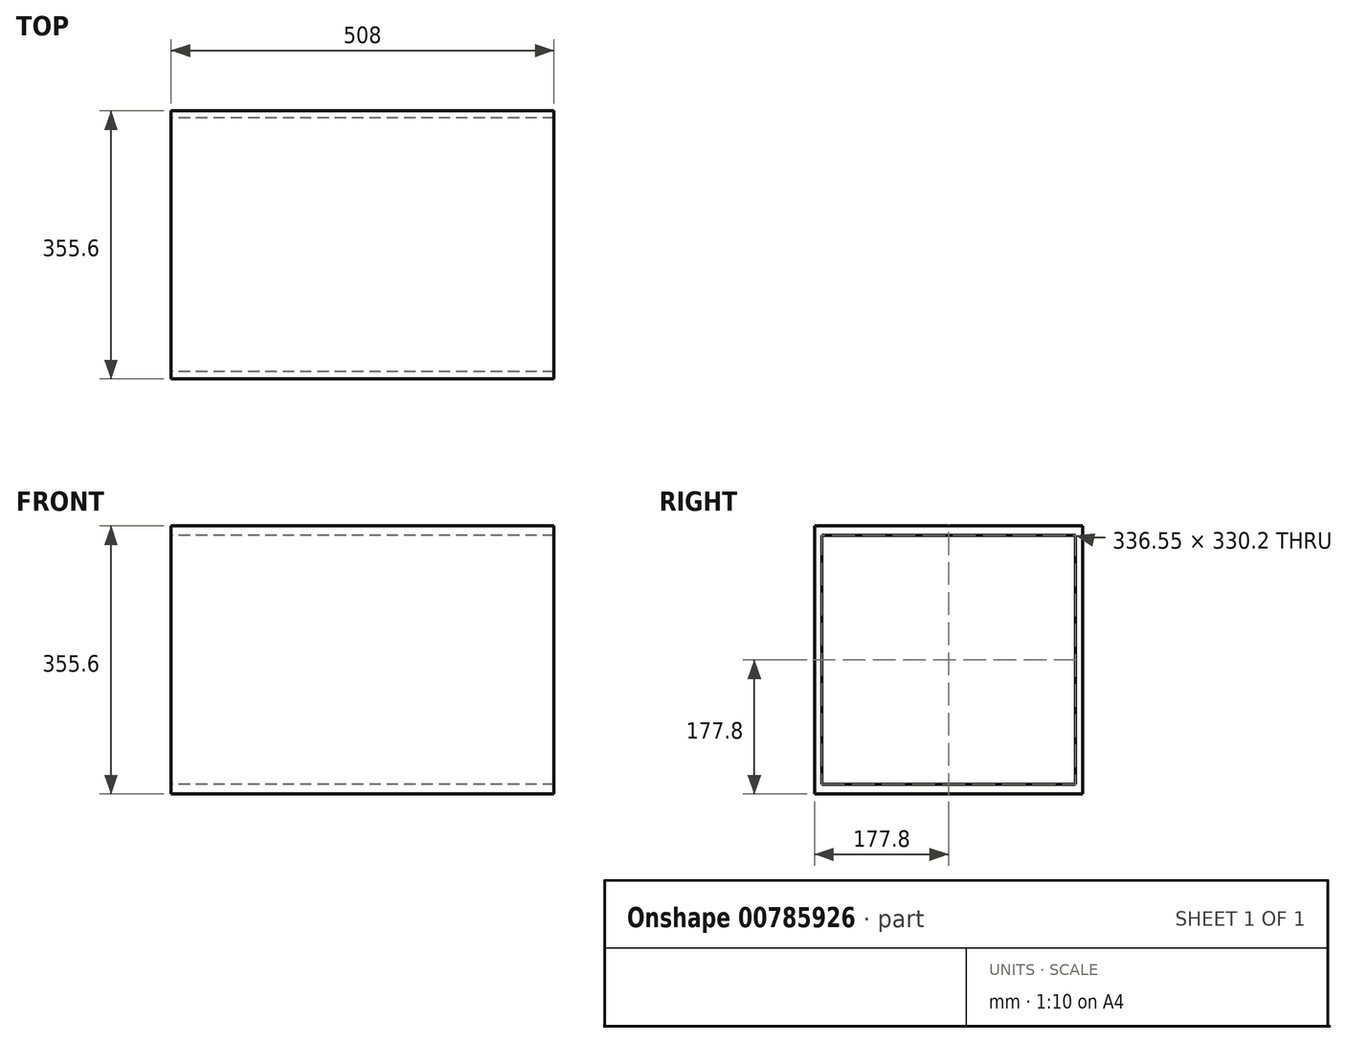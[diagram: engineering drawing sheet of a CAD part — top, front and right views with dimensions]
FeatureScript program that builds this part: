
annotation { "Feature Type Name" : "Feature", "Feature Type Description" : "" }
export const myFeature = defineFeature(function(context is Context, id is Id, definition is map)
    precondition{}
    {
        {
            var Q0;
            Q0=qCreatedBy(makeId("Right.planeOp"),FACE);
            var sketch = newSketch(context, id + "F0", { "sketchPlane" : qUnion([Q0])});
            skLineSegment(sketch, "E0.bottom", {"start": v(-168.28, -165.1) * mm, "end": v(168.28, -165.1) * mm});
            skLineSegment(sketch, "E0.top", {"start": v(-168.28, 165.1) * mm, "end": v(168.28, 165.1) * mm});
            skLineSegment(sketch, "E0.left", {"start": v(-168.28, -165.1) * mm, "end": v(-168.28, 165.1) * mm});
            skLineSegment(sketch, "E0.right", {"start": v(168.28, -165.1) * mm, "end": v(168.28, 165.1) * mm});
            skPoint(sketch, "E0.middle", {"position": v(0, 0) * mm});
            skLineSegment(sketch, "E1.bottom", {"start": v(-177.8, -177.8) * mm, "end": v(177.8, -177.8) * mm});
            skLineSegment(sketch, "E1.top", {"start": v(-177.8, 177.8) * mm, "end": v(177.8, 177.8) * mm});
            skLineSegment(sketch, "E1.left", {"start": v(-177.8, -177.8) * mm, "end": v(-177.8, 177.8) * mm});
            skLineSegment(sketch, "E1.right", {"start": v(177.8, -177.8) * mm, "end": v(177.8, 177.8) * mm});
            skSolve(sketch);
        }
        {
            var Q0;
            Q0 = qSketchRegion(id + "F0", true);
            extrude(context, id + "F1", {"entities" : qUnion([Q0]), "endBound" : BoundingType.SYMMETRIC, "depth" : 508 * mm, "offsetDistance" : 25.4 * mm});
        }
    });
